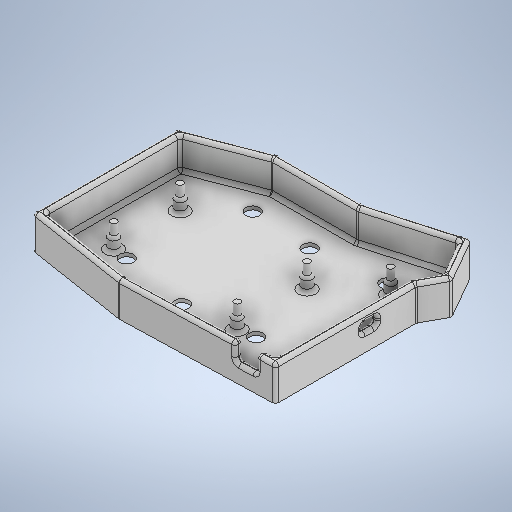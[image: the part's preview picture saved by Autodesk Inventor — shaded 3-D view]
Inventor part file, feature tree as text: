
AUTODESK INVENTOR PART (.ipt)
format: ipt  version: 2025 (Build 290162000, 162)  size: 569,856 bytes
history: native  units: mm
features: extrude x7, sketch x5, other x1, fillet x1
ambient origin geometry x8: Origin, YZ Plane, XZ Plane, XY Plane, X Axis, Y Axis, Z Axis, Center Point
bodies: Body1 (feature_tree)
feature tree (14):
  other  "Твердое тело1"
  sketch  "Эскиз1"
  sketch  "Эскиз2"
  sketch  "Эскиз3"
  extrude  "Выдавливание1"  Depth=2.0mm
  extrude  "Выдавливание2"  Depth=2.0mm
  extrude  "Выдавливание3"  Depth=5.0mm
  extrude  "Выдавливание4"  Depth=5.0mm
  extrude  "Выдавливание5"  Depth=6.0mm
  extrude  "Выдавливание6"  Depth=6.0mm
  extrude  "Выдавливание7"  Depth=6.0mm
  fillet  "Сопряжение1"  Radius=6.0mm
  sketch  "Эскиз4"
  sketch  "Эскиз5"
